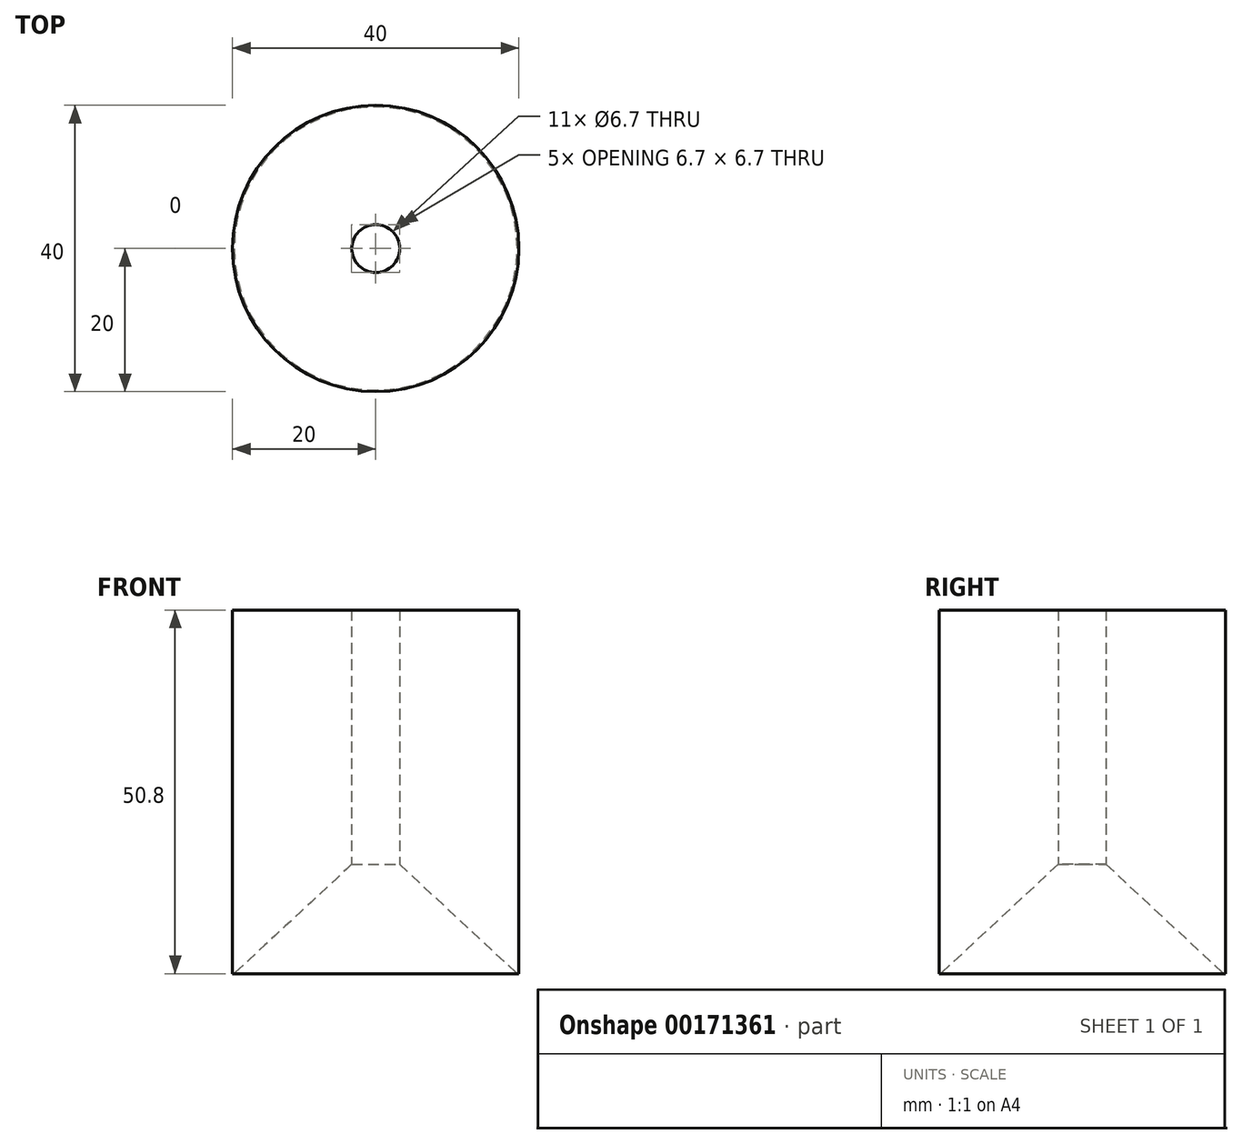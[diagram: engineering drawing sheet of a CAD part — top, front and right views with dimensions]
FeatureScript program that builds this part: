
annotation { "Feature Type Name" : "Feature", "Feature Type Description" : "" }
export const myFeature = defineFeature(function(context is Context, id is Id, definition is map)
    precondition{}
    {
        {
            var Q0;
            Q0=qCreatedBy(makeId("Top.planeOp"),FACE);
            var sketch = newSketch(context, id + "F0", { "sketchPlane" : qUnion([Q0])});
            skCircle(sketch, "E0", {"center": v(0, 0) * mm, "radius": 20 * mm});
            skCircle(sketch, "E1", {"center": v(0, 0) * mm, "radius": 3.35 * mm});
            skSolve(sketch);
        }
        {
            var Q0;
            Q0 = qSketchRegion(id + "F0", true);
            extrude(context, id + "F1", {"entities" : qUnion([Q0]), "depth" : 50.8 * mm});
        }
        {
            var Q0;
            Q0=qCreatedBy(makeId("Right.planeOp"),FACE);
            var sketch = newSketch(context, id + "F2", { "sketchPlane" : qUnion([Q0])});
            skLineSegment(sketch, "E2", {"start": v(-19.77, 0) * mm, "end": v(0, 18.37) * mm});
            skLineSegment(sketch, "E3", {"start": v(0, 18.37) * mm, "end": v(0, 0) * mm});
            skLineSegment(sketch, "E4", {"start": v(0, 0) * mm, "end": v(-19.77, 0) * mm});
            skSolve(sketch);
        }
        {
            var Q0;
            Q0 = qSketchRegion(id + "F2", true);
            var Q1;
            Q1=sQuery(id+"F2.wireOp",EDGE,"E3");
            revolve(context, id + "F3", {"operationType" : NewBodyOperationType.REMOVE, "entities" : qUnion([Q0]), "axis" : qUnion([Q1]), "revolveType" : RevolveType.FULL, "oppositeDirection" : true});
        }
    });
